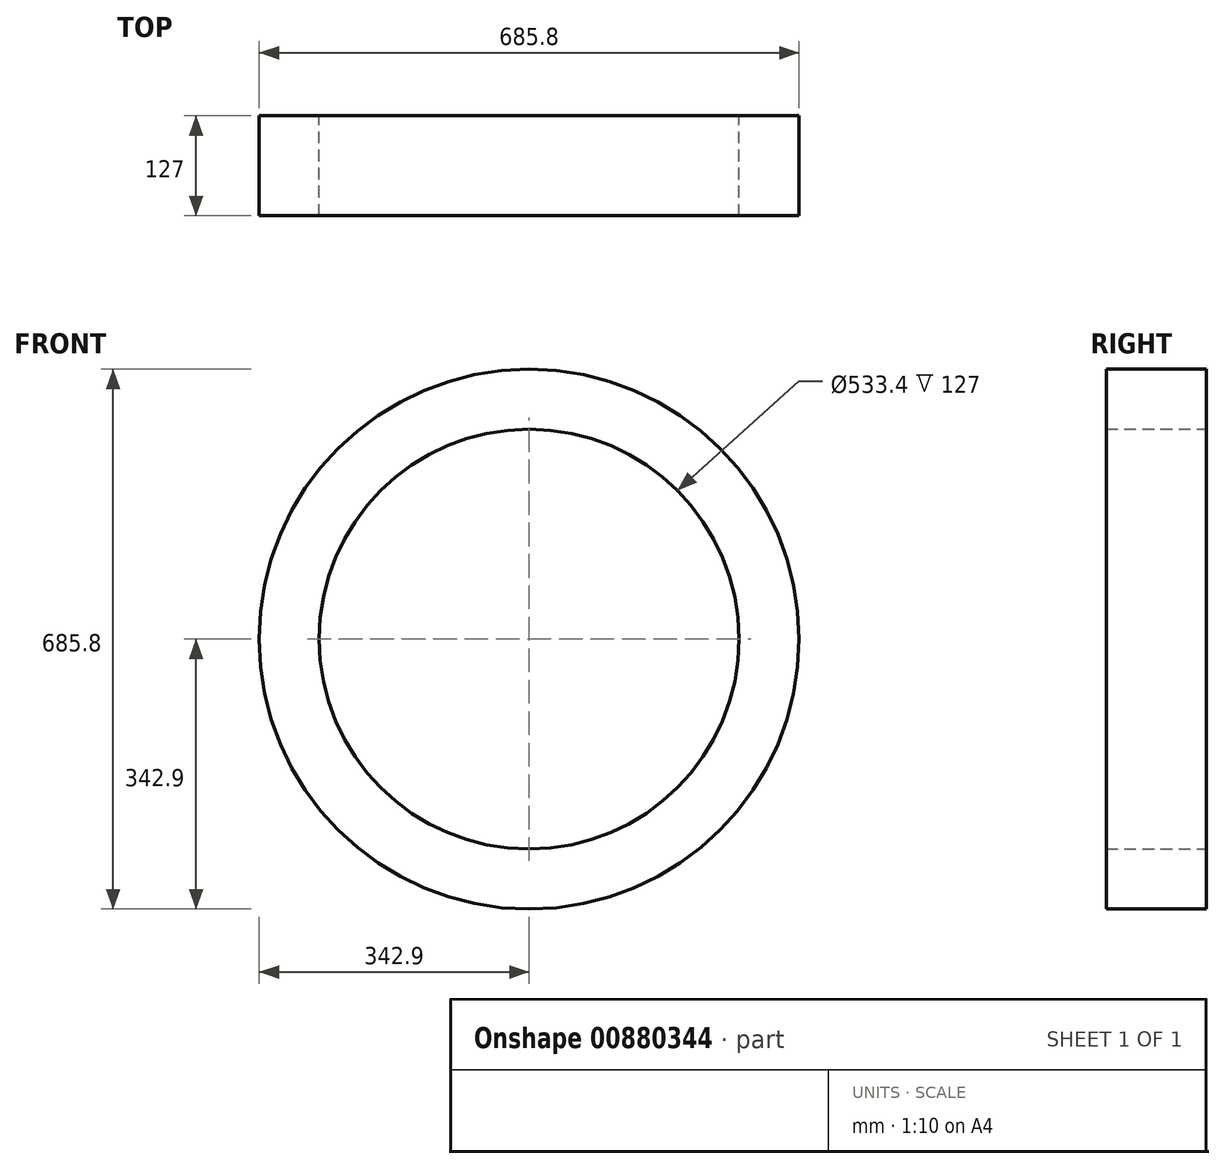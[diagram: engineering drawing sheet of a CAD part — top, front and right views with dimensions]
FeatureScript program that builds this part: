
annotation { "Feature Type Name" : "Feature", "Feature Type Description" : "" }
export const myFeature = defineFeature(function(context is Context, id is Id, definition is map)
    precondition{}
    {
        {
            var Q0;
            Q0=qCreatedBy(makeId("Front.planeOp"),FACE);
            var sketch = newSketch(context, id + "F0", { "sketchPlane" : qUnion([Q0])});
            skCircle(sketch, "E0", {"center": v(0, 0) * mm, "radius": 266.7 * mm});
            skCircle(sketch, "E1", {"center": v(0, 0) * mm, "radius": 342.9 * mm});
            skSolve(sketch);
        }
        {
            var Q0;
            Q0 = qSketchRegion(id + "F0", true);
            extrude(context, id + "F1", {"entities" : qUnion([Q0]), "depth" : 127 * mm, "offsetDistance" : 25 * mm});
        }
    });
